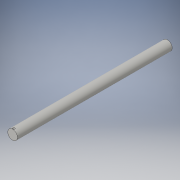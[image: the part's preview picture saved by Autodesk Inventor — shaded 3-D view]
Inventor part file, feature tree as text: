
AUTODESK INVENTOR PART (.ipt)
format: ipt  version: 2016 (Build 200138000, 138)  size: 98,304 bytes
history: native  units: in
note: dims shown in document units (in); Inventor stores cm internally (conversion verified against a paired STEP export)
features: extrude x2, sketch x1
ambient origin geometry x8: Origin, YZ Plane, XZ Plane, XY Plane, X Axis, Y Axis, Z Axis, Center Point
bodies: Solid1 (feature_tree)
feature tree (3):
  extrude  "Extrusion1"  Depth=8.0in TaperAngle=0.0deg
  extrude  "Extrusion7"  Depth=8.0in
  sketch  "Sketch1"  dims[d0=0.5in d1=8.0in d2=0.0in d15=0.06in d16=0.1in d33=1.0in d34=0.0in]
